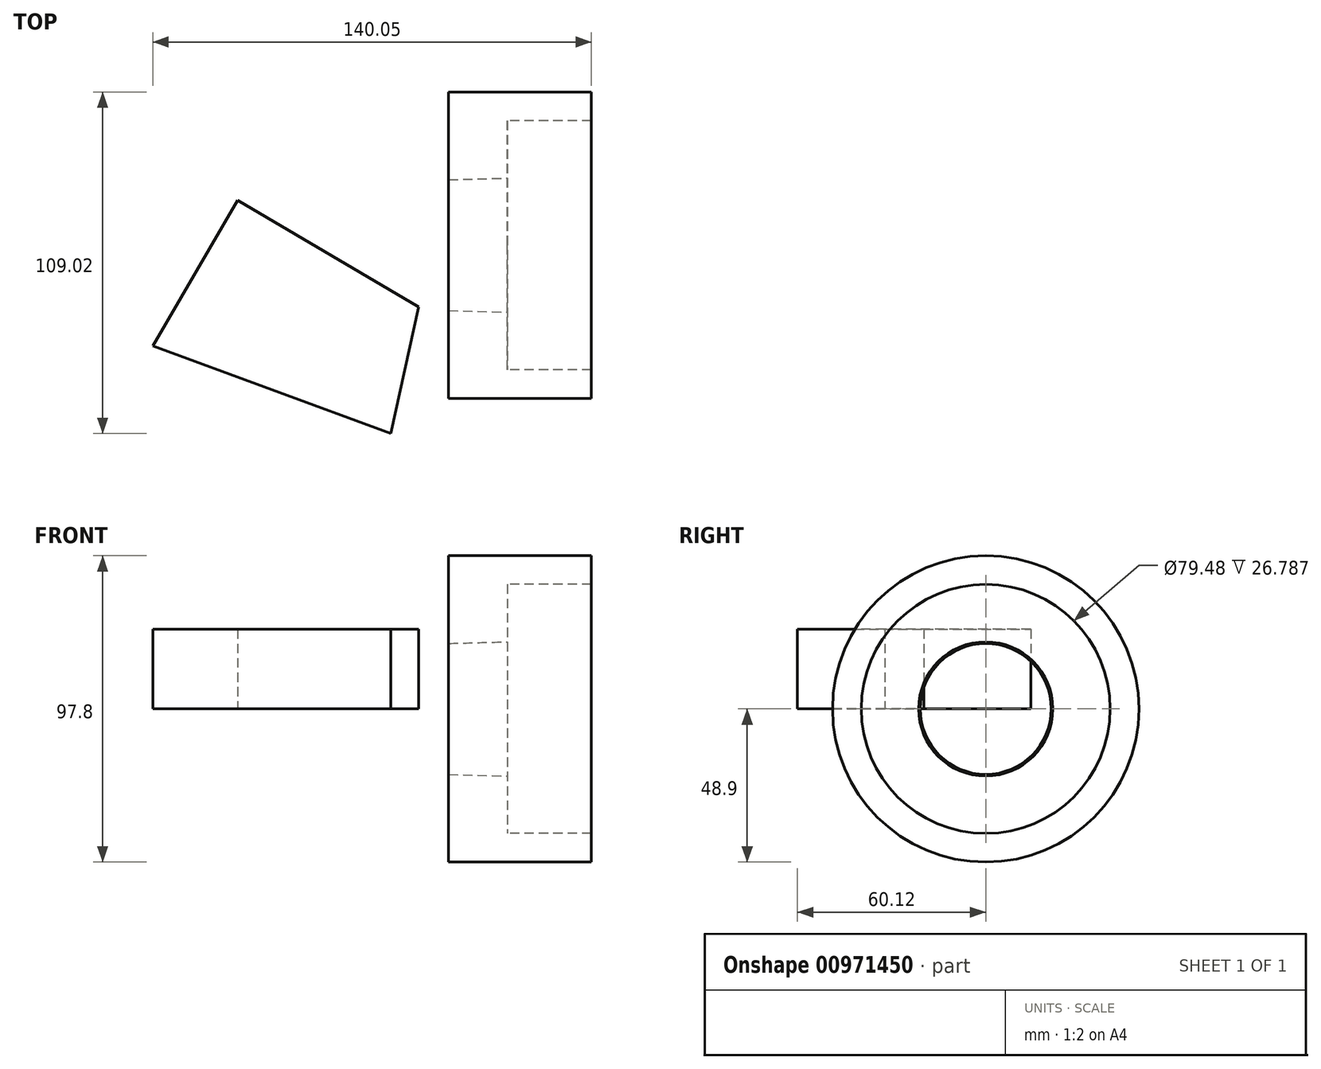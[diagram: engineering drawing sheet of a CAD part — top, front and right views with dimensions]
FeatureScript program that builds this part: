
annotation { "Feature Type Name" : "Feature", "Feature Type Description" : "" }
export const myFeature = defineFeature(function(context is Context, id is Id, definition is map)
    precondition{}
    {
        {
            var Q0;
            Q0=qCreatedBy(makeId("Top.planeOp"),FACE);
            var sketch = newSketch(context, id + "F0", { "sketchPlane" : qUnion([Q0])});
            skLineSegment(sketch, "E0", {"start": v(-94.45, -32.15) * mm, "end": v(-18.4, -60.12) * mm});
            skLineSegment(sketch, "E1", {"start": v(-18.4, -60.12) * mm, "end": v(-9.58, -19.72) * mm});
            skLineSegment(sketch, "E2", {"start": v(-9.58, -19.72) * mm, "end": v(-67.4, 14.36) * mm});
            skLineSegment(sketch, "E3", {"start": v(-67.4, 14.36) * mm, "end": v(-94.45, -32.15) * mm});
            skSolve(sketch);
        }
        {
            var Q0;
            Q0 = qSketchRegion(id + "F0", true);
            extrude(context, id + "F1", {"entities" : qUnion([Q0]), "depth" : 25.4 * mm, "offsetDistance" : 25.4 * mm});
        }
        {
            var Q0;
            Q0=qCreatedBy(makeId("Front.planeOp"),FACE);
            var sketch = newSketch(context, id + "F2", { "sketchPlane" : qUnion([Q0])});
            skLineSegment(sketch, "E4", {"start": v(0, 20.9) * mm, "end": v(0, 48.9) * mm});
            skLineSegment(sketch, "E5", {"start": v(0, 48.9) * mm, "end": v(45.6, 48.9) * mm});
            skLineSegment(sketch, "E6", {"start": v(45.6, 48.9) * mm, "end": v(45.6, 39.74) * mm});
            skLineSegment(sketch, "E7", {"start": v(45.6, 39.74) * mm, "end": v(18.8, 39.74) * mm});
            skLineSegment(sketch, "E8", {"start": v(18.8, 39.74) * mm, "end": v(18.8, 21.41) * mm});
            skLineSegment(sketch, "E9", {"start": v(18.8, 21.41) * mm, "end": v(0, 20.9) * mm});
            skLineSegment(sketch, "E10", {"start": v(0, 0) * mm, "end": v(39.51, 0) * mm, "construction": true});
            skSolve(sketch);
        }
        {
            var Q0;
            Q0 = qSketchRegion(id + "F2", true);
            var Q1;
            Q1=sQuery(id+"F2.wireOp",EDGE,"E10");
            revolve(context, id + "F3", {"surfaceOperationType" : NewSurfaceOperationType.NEW, "entities" : qUnion([Q0]), "axis" : qUnion([Q1]), "revolveType" : RevolveType.FULL});
        }
    });
